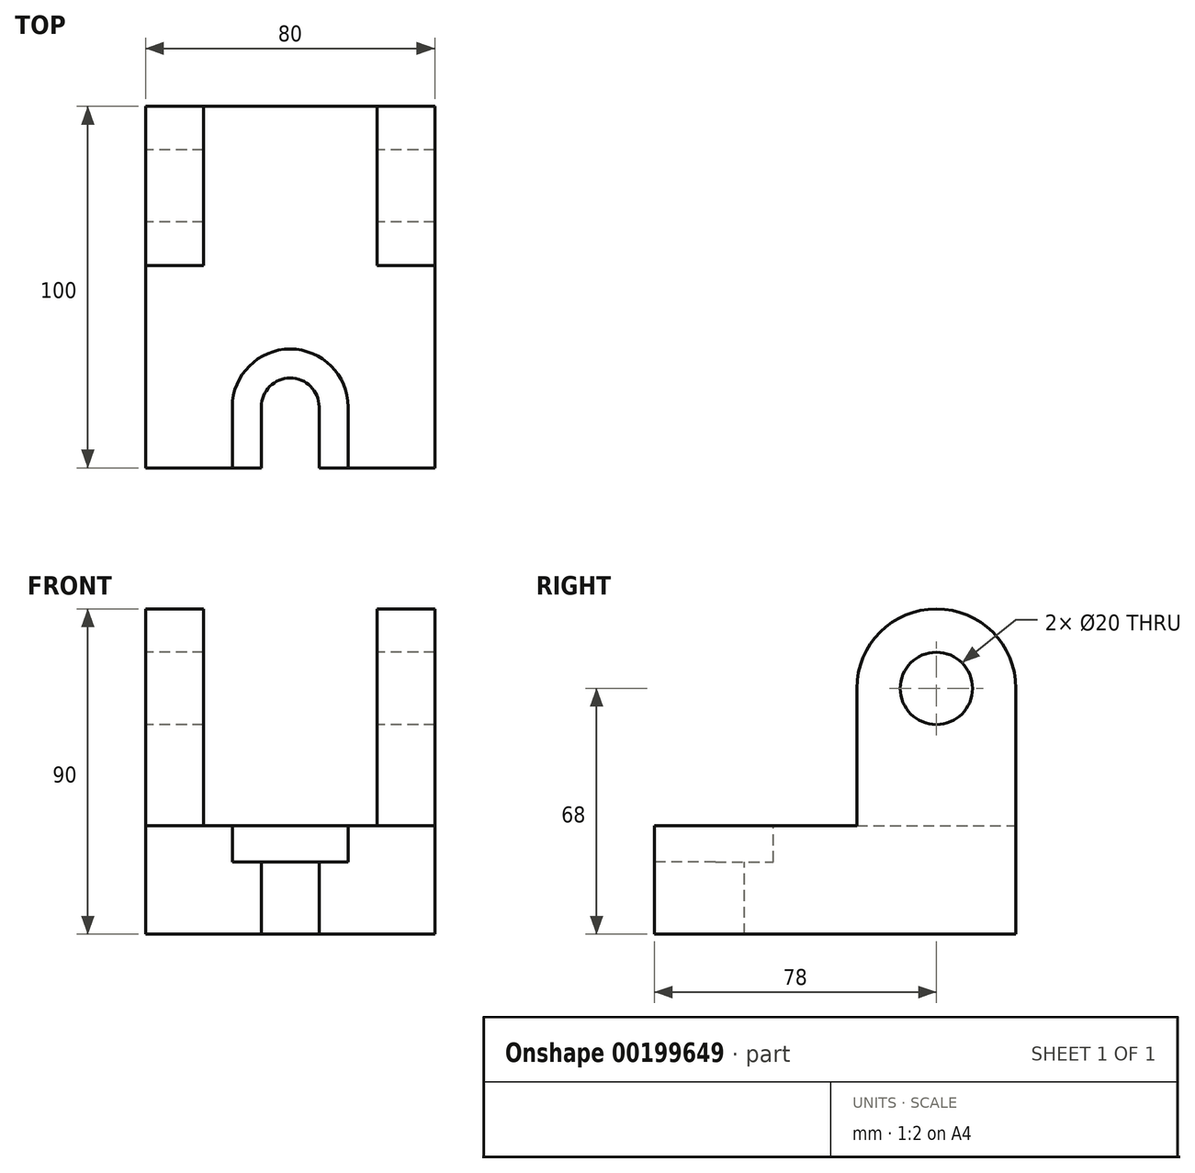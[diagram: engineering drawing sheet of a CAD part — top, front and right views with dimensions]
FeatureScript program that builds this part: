
annotation { "Feature Type Name" : "Feature", "Feature Type Description" : "" }
export const myFeature = defineFeature(function(context is Context, id is Id, definition is map)
    precondition{}
    {
        {
            var Q0;
            Q0=qCreatedBy(makeId("Right.planeOp"),FACE);
            var sketch = newSketch(context, id + "F0", { "sketchPlane" : qUnion([Q0])});
            skLineSegment(sketch, "E0", {"start": v(0, 0) * mm, "end": v(0, 68) * mm});
            skLineSegment(sketch, "E1", {"start": v(0, 68) * mm, "end": v(-44, 68) * mm});
            skLineSegment(sketch, "E2", {"start": v(-44, 68) * mm, "end": v(-44, 30) * mm});
            skLineSegment(sketch, "E3", {"start": v(-44, 30) * mm, "end": v(-100, 30) * mm});
            skLineSegment(sketch, "E4", {"start": v(-100, 30) * mm, "end": v(-100, 0) * mm});
            skLineSegment(sketch, "E5", {"start": v(-100, 0) * mm, "end": v(0, 0) * mm});
            skCircle(sketch, "E6", {"center": v(-22, 68) * mm, "radius": 22 * mm});
            skCircle(sketch, "E7", {"center": v(-22, 68) * mm, "radius": 10 * mm});
            skLineSegment(sketch, "E8", {"start": v(-44, 30) * mm, "end": v(0, 30) * mm});
            skSolve(sketch);
        }
        {
            var Q0;
            Q0 = qSketchRegion(id + "F0", true);
            extrude(context, id + "F1", {"entities" : qUnion([Q0]), "endBound" : BoundingType.SYMMETRIC, "depth" : 80 * mm});
        }
        {
            var Q0;
            {var subQ5=sQuery(id+"F0.wireOp",EDGE,"E2");Q0=makeQuery(id+"F0.imprint","IMPRINT",FACE,{"disambiguationData":[TD([[makeQuery(id+"F0.imprint","IMPRINT",EDGE,{"derivedFrom":subQ5}),1.0]])]});}
            var Q1;
            {var subQ1=sQuery(id+"F0.wireOp",EDGE,"E1");var subQ3=sQuery(id+"F0.wireOp",EDGE,"E7");var subQ4=makeQuery(id+"F0.imprint","INTERSECT",VERTEX,{"disambiguationData":[OD(0.0)],"derivedFrom":[subQ1,subQ3]});Q1=makeQuery(id+"F0.imprint","IMPRINT",FACE,{"disambiguationData":[TD([[makeQuery(id+"F0.imprint","IMPRINT",EDGE,{"disambiguationData":[TD([[subQ4,1.0]])],"derivedFrom":subQ3}),-1.0]])]});}
            var Q2;
            {var subQ1=sQuery(id+"F0.wireOp",EDGE,"E1");var subQ3=sQuery(id+"F0.wireOp",EDGE,"E7");var subQ4=makeQuery(id+"F0.imprint","INTERSECT",VERTEX,{"disambiguationData":[OD(0.0)],"derivedFrom":[subQ1,subQ3]});Q2=makeQuery(id+"F0.imprint","IMPRINT",FACE,{"disambiguationData":[TD([[makeQuery(id+"F0.imprint","IMPRINT",EDGE,{"disambiguationData":[TD([[subQ4,-1.0]])],"derivedFrom":subQ3}),-1.0]])]});}
            var Q3;
            {var subQ0=sQuery(id+"F0.wireOp",EDGE,"E7");var subQ1=sQuery(id+"F0.wireOp",EDGE,"E1");var subQ2=makeQuery(id+"F0.imprint","INTERSECT",VERTEX,{"disambiguationData":[OD(0.0)],"derivedFrom":[subQ1,subQ0]});Q3=makeQuery(id+"F0.imprint","IMPRINT",FACE,{"disambiguationData":[TD([[makeQuery(id+"F0.imprint","IMPRINT",EDGE,{"disambiguationData":[TD([[subQ2,-1.0]])],"derivedFrom":subQ1}),-1.0]])]});}
            extrude(context, id + "F2", {"entities" : qUnion([Q0, Q1, Q2, Q3]), "operationType" : NewBodyOperationType.REMOVE, "endBound" : BoundingType.SYMMETRIC, "depth" : 48 * mm});
        }
        {
            var Q0;
            Q0=makeQuery(id+"F2.boolean.opBoolean","MERGE",FACE,{"derivedFrom":[makeQuery(id+"F1.opExtrude","SWEPT_FACE",FACE,{"disambiguationData":[OSD([sQuery(id+"F0.wireOp",EDGE,"E3")])]}),makeQuery(id+"F2.opExtrude","SWEPT_FACE",FACE,{"disambiguationData":[OSD([sQuery(id+"F0.wireOp",EDGE,"E8")])]})]});
            var sketch = newSketch(context, id + "F3", { "sketchPlane" : qUnion([Q0])});
            skPoint(sketch, "E9.startSnap0", {"position": v(0, -100) * mm});
            skLineSegment(sketch, "E10", {"start": v(16, -83.14) * mm, "end": v(16, -100) * mm});
            skLineSegment(sketch, "E11", {"start": v(-16, -83.14) * mm, "end": v(-16, -100) * mm});
            skArc(sketch, "E12", {"start": v(16, -83.14) * mm, "mid": v(0, -67.14) * mm, "end": v(-16, -83.14) * mm});
            skLineSegment(sketch, "E13.0", {"start": v(-8, -83.14) * mm, "end": v(-8, -100) * mm});
            skArc(sketch, "E13.1", {"start": v(8, -83.14) * mm, "mid": v(0, -75.14) * mm, "end": v(-8, -83.14) * mm});
            skLineSegment(sketch, "E13.2", {"start": v(8, -83.14) * mm, "end": v(8, -100) * mm});
            skSolve(sketch);
        }
        {
            var Q0;
            {var subQ2=sQuery(id+"F3.wireOp",EDGE,"E10");Q0=makeQuery(id+"F3.imprint","IMPRINT",FACE,{"disambiguationData":[TD([[makeQuery(id+"F3.imprint","IMPRINT",EDGE,{"derivedFrom":subQ2}),-1.0]])]});}
            extrude(context, id + "F4", {"entities" : qUnion([Q0]), "operationType" : NewBodyOperationType.REMOVE, "oppositeDirection" : true, "depth" : 10 * mm});
        }
        {
            var Q0;
            Q0=makeQuery(id+"F4.boolean.opBoolean","SPLIT",FACE,{"disambiguationData":[TD([makeQuery(id+"F4.opExtrude","SWEPT_FACE",FACE,{"disambiguationData":[OSD([sQuery(id+"F3.wireOp",EDGE,"E13.0")])]})])],"derivedFrom":makeQuery(id+"F2.boolean.opBoolean","MERGE",FACE,{"derivedFrom":[makeQuery(id+"F1.opExtrude","SWEPT_FACE",FACE,{"disambiguationData":[OSD([sQuery(id+"F0.wireOp",EDGE,"E3")])]}),makeQuery(id+"F2.opExtrude","SWEPT_FACE",FACE,{"disambiguationData":[OSD([sQuery(id+"F0.wireOp",EDGE,"E8")])]})]})});
            extrude(context, id + "F5", {"entities" : qUnion([Q0]), "operationType" : NewBodyOperationType.REMOVE, "endBound" : BoundingType.THROUGH_ALL, "oppositeDirection" : true, "depth" : 25 * mm});
        }
    });
